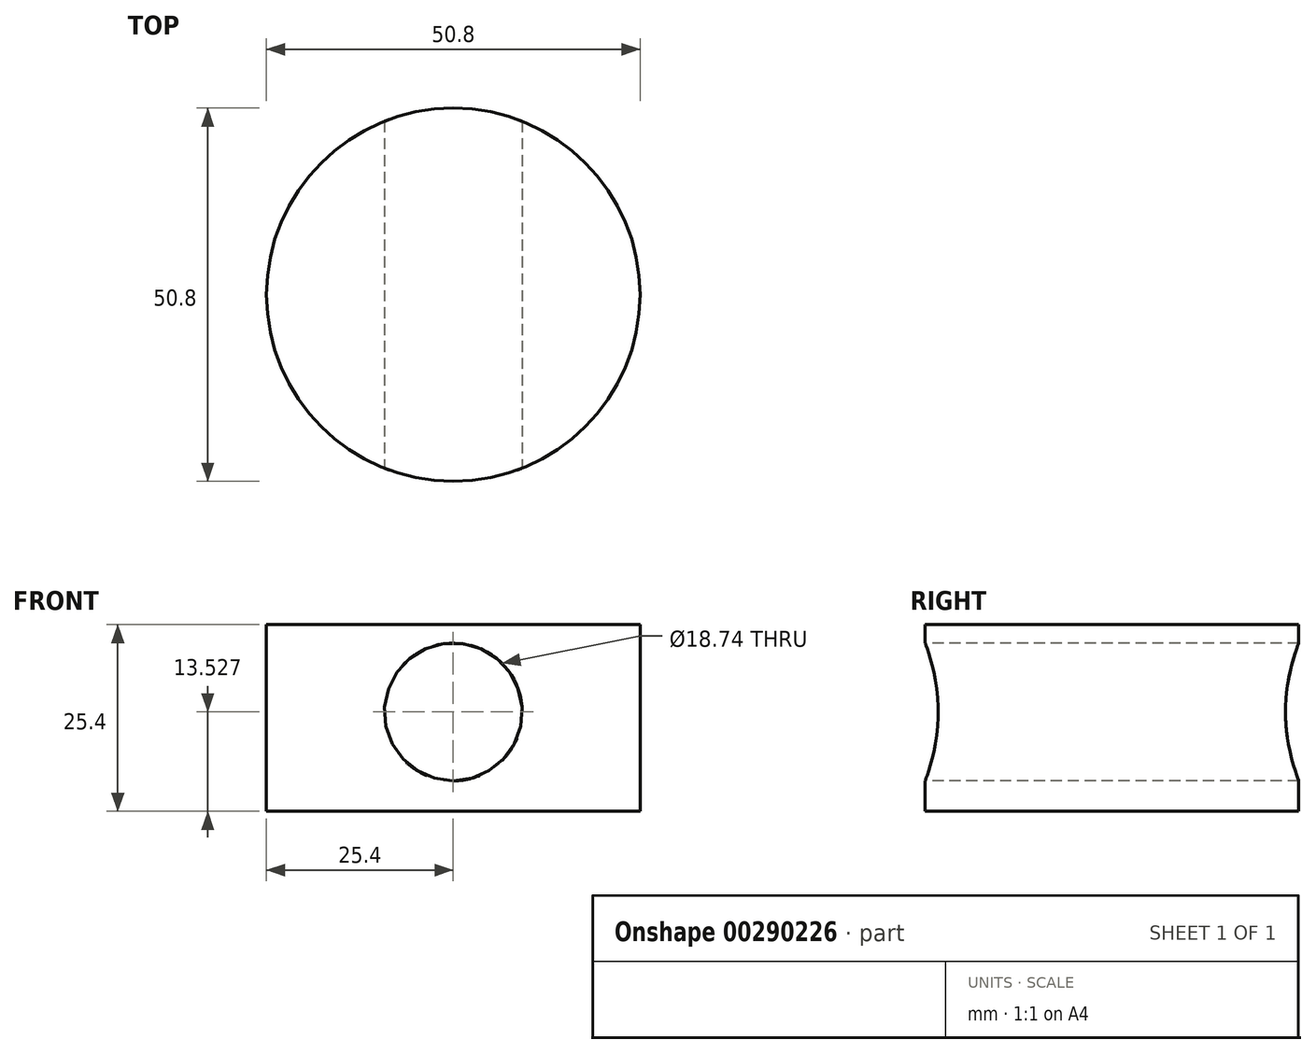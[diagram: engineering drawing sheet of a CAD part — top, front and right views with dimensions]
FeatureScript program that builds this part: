
annotation { "Feature Type Name" : "Feature", "Feature Type Description" : "" }
export const myFeature = defineFeature(function(context is Context, id is Id, definition is map)
    precondition{}
    {
        {
            var Q0;
            Q0=qCreatedBy(makeId("Top.planeOp"),FACE);
            var sketch = newSketch(context, id + "F0", { "sketchPlane" : qUnion([Q0])});
            skCircle(sketch, "E0", {"center": v(0, 0) * mm, "radius": 25.4 * mm});
            skSolve(sketch);
        }
        {
            var Q0;
            Q0 = qSketchRegion(id + "F0", true);
            extrude(context, id + "F1", {"entities" : qUnion([Q0]), "depth" : 25.4 * mm});
        }
        {
            var Q0;
            Q0=qCreatedBy(makeId("Front.planeOp"),FACE);
            var sketch = newSketch(context, id + "F2", { "sketchPlane" : qUnion([Q0])});
            skCircle(sketch, "E1", {"center": v(0, 13.53) * mm, "radius": 9.37 * mm});
            skSolve(sketch);
        }
        {
            var Q0;
            Q0=makeQuery(id+"F2.imprint","IMPRINT",FACE,{"disambiguationData":[TD([[makeQuery(id+"F2.imprint","IMPRINT",EDGE,{"derivedFrom":sQuery(id+"F2.wireOp",EDGE,"E1")}),1.0]])]});
            extrude(context, id + "F3", {"entities" : qUnion([Q0]), "operationType" : NewBodyOperationType.REMOVE, "endBound" : BoundingType.SYMMETRIC, "oppositeDirection" : true, "depth" : 104.14 * mm});
        }
    });
